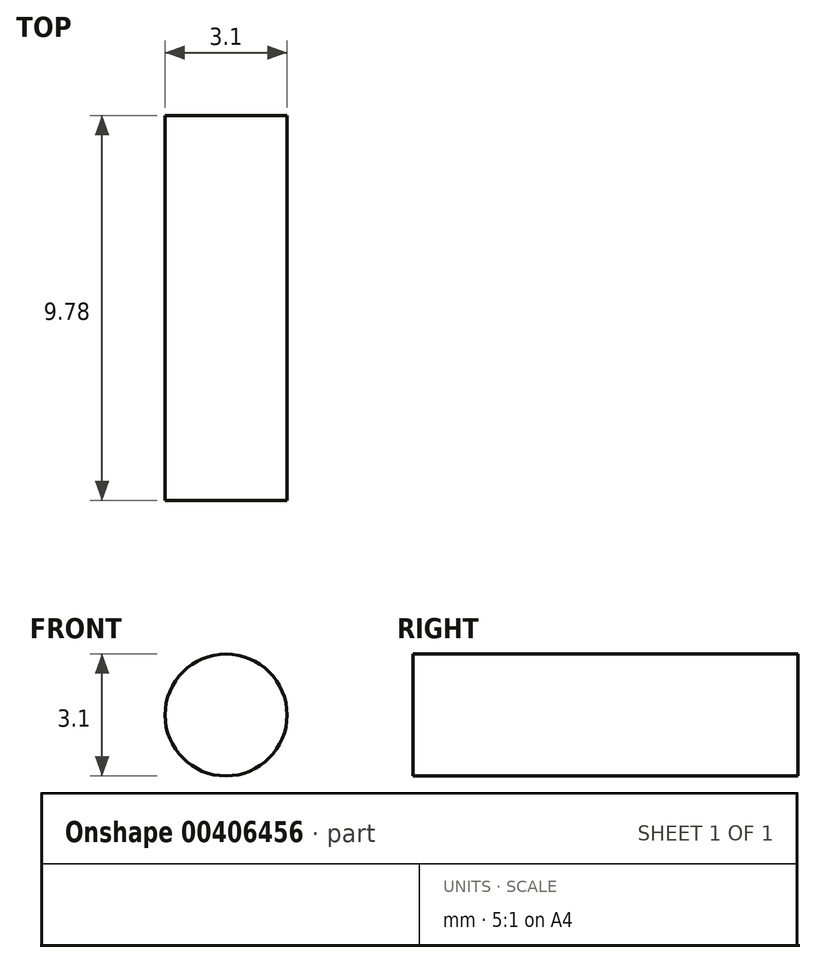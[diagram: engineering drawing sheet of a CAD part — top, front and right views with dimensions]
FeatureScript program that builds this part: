
annotation { "Feature Type Name" : "Feature", "Feature Type Description" : "" }
export const myFeature = defineFeature(function(context is Context, id is Id, definition is map)
    precondition{}
    {
        {
            var Q0;
            Q0=qCreatedBy(makeId("Front.planeOp"),FACE);
            var sketch = newSketch(context, id + "F0", { "sketchPlane" : qUnion([Q0])});
            skCircle(sketch, "E0", {"center": v(0, 0) * mm, "radius": 1.55 * mm});
            skSolve(sketch);
        }
        {
            var Q0;
            Q0 = qSketchRegion(id + "F0", true);
            extrude(context, id + "F1", {"entities" : qUnion([Q0]), "depth" : 9.78 * mm});
        }
    });
